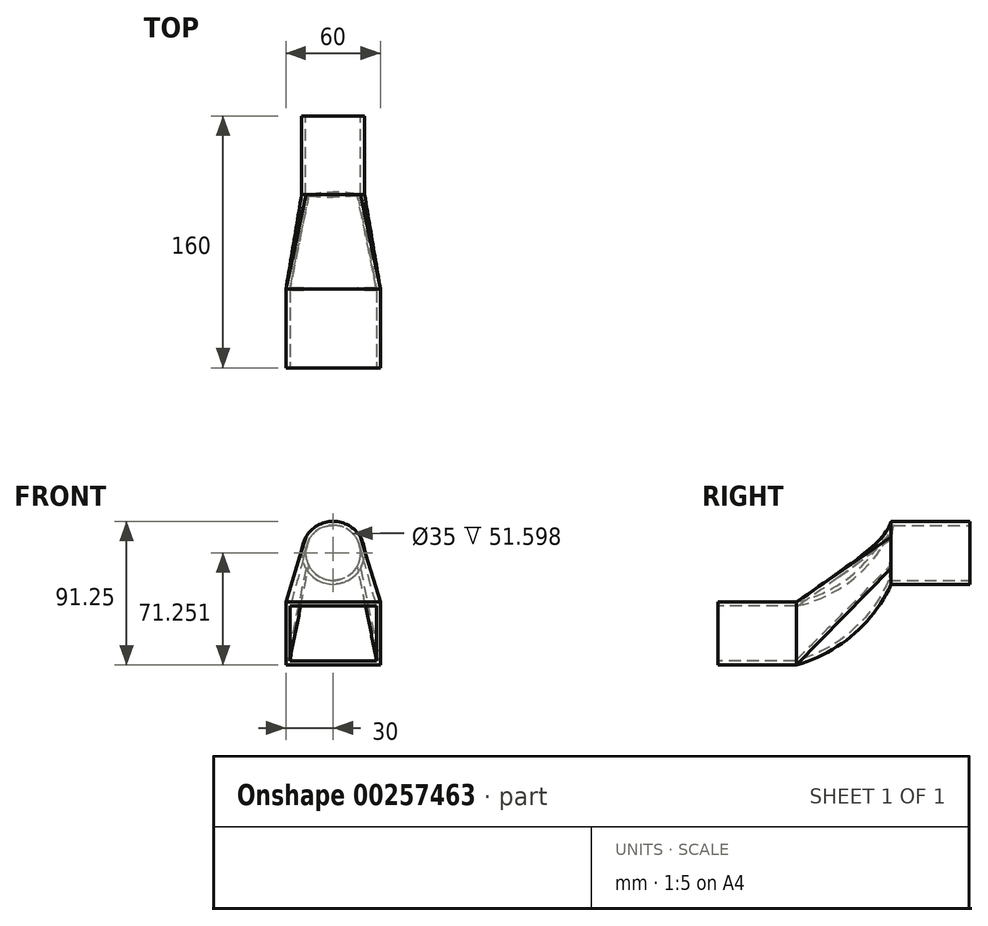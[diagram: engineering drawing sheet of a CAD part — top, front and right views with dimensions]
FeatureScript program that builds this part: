
annotation { "Feature Type Name" : "Feature", "Feature Type Description" : "" }
export const myFeature = defineFeature(function(context is Context, id is Id, definition is map)
    precondition{}
    {
        {
            var Q0;
            Q0=qCreatedBy(makeId("Front.planeOp"),FACE);
            var sketch = newSketch(context, id + "F0", { "sketchPlane" : qUnion([Q0])});
            skLineSegment(sketch, "E0.bottom", {"start": v(30, -20) * mm, "end": v(-30, -20) * mm});
            skLineSegment(sketch, "E0.top", {"start": v(30, 20) * mm, "end": v(-30, 20) * mm});
            skLineSegment(sketch, "E0.left", {"start": v(30, -20) * mm, "end": v(30, 20) * mm});
            skLineSegment(sketch, "E0.right", {"start": v(-30, -20) * mm, "end": v(-30, 20) * mm});
            skPoint(sketch, "E0.middle", {"position": v(0, 0) * mm});
            skSolve(sketch);
        }
        {
            var Q0;
            Q0=makeQuery(id+"F0.imprint","IMPRINT",FACE,{"disambiguationData":[TD([[makeQuery(id+"F0.imprint","IMPRINT",EDGE,{"derivedFrom":sQuery(id+"F0.wireOp",EDGE,"E0.bottom")}),-1.0]])]});
            extrude(context, id + "F1", {"entities" : qUnion([Q0]), "oppositeDirection" : true, "depth" : 50 * mm});
        }
        {
            var Q0;
            Q0=qCreatedBy(makeId("Front.planeOp"),FACE);
            cPlane(context, id + "F2", {"entities" : qUnion([Q0]), "cplaneType" : CPlaneType.OFFSET, "offset" : 160 * mm, "oppositeDirection" : true, "width" : 150 * mm, "height" : 150 * mm});
        }
        {
            var Q0;
            Q0=qCreatedBy(id+"F2.planeOp",FACE);
            var sketch = newSketch(context, id + "F3", { "sketchPlane" : qUnion([Q0])});
            skLineSegment(sketch, "E1.0", {"start": v(30, 20) * mm, "end": v(-30, 20) * mm, "construction": true});
            skCircle(sketch, "E2", {"center": v(0, 51.25) * mm, "radius": 20 * mm});
            skSolve(sketch);
        }
        {
            var Q0;
            Q0=makeQuery(id+"F3.imprint","IMPRINT",FACE,{"disambiguationData":[TD([[makeQuery(id+"F3.imprint","IMPRINT",EDGE,{"derivedFrom":sQuery(id+"F3.wireOp",EDGE,"E2")}),1.0]])]});
            extrude(context, id + "F4", {"entities" : qUnion([Q0]), "depth" : 50 * mm});
        }
        {
            var Q0;
            Q0=qCreatedBy(makeId("Right.planeOp"),FACE);
            var sketch = newSketch(context, id + "F5", { "sketchPlane" : qUnion([Q0])});
            skLineSegment(sketch, "E3.0.0", {"start": v(110, 31.25) * mm, "end": v(110, 71.25) * mm, "construction": true});
            skLineSegment(sketch, "E3.1.0", {"start": v(50, 20) * mm, "end": v(50, -20) * mm, "construction": true});
            skLineSegment(sketch, "E3.1.2", {"start": v(50, -20) * mm, "end": v(50, 20) * mm, "construction": true});
            skArc(sketch, "E4", {"start": v(50, 20) * mm, "mid": v(86.34, 38.2) * mm, "end": v(110, 71.25) * mm});
            skArc(sketch, "E5", {"start": v(50, -20) * mm, "mid": v(85.6, -0.93) * mm, "end": v(110, 31.25) * mm});
            skSolve(sketch);
        }
        {
            var Q1;
            Q1=makeQuery(id+"F4.opExtrude","CAP_FACE",FACE,{"disambiguationData":[OSD([sQuery(id+"F3.wireOp",EDGE,"E2")])],"isStart":false});
            var Q2;
            Q2=makeQuery(id+"F1.opExtrude","CAP_FACE",FACE,{"disambiguationData":[OSD([sQuery(id+"F0.wireOp",EDGE,"E0.bottom"),sQuery(id+"F0.wireOp",EDGE,"E0.top"),sQuery(id+"F0.wireOp",EDGE,"E0.left"),sQuery(id+"F0.wireOp",EDGE,"E0.right")])],"isStart":false});
            var Q3;
            Q3=sQuery(id+"F5.wireOp",EDGE,"E4");
            var Q4;
            Q4=sQuery(id+"F5.wireOp",EDGE,"E5");
            loft(context, id + "F6", {"operationType" : NewBodyOperationType.ADD, "addGuides" : true, "sheetProfilesArray" : [{ "sheetProfileEntities" : qUnion([Q1]) }, { "sheetProfileEntities" : qUnion([Q2]) }], "guidesArray" : [{ "guideEntities" : qUnion([Q3]), "guideDerivativeType" : LoftGuideDerivativeType.DEFAULT, "guideDerivativeMagnitude" : 1 }, { "guideEntities" : qUnion([Q4]), "guideDerivativeType" : LoftGuideDerivativeType.DEFAULT, "guideDerivativeMagnitude" : 1 }]});
        }
        {
            var Q0;
            Q0=makeQuery(id+"F4.opExtrude","CAP_FACE",FACE,{"disambiguationData":[OSD([sQuery(id+"F3.wireOp",EDGE,"E2")])],"isStart":true});
            var Q1;
            Q1=makeQuery(id+"F1.opExtrude","CAP_FACE",FACE,{"disambiguationData":[OSD([sQuery(id+"F0.wireOp",EDGE,"E0.bottom"),sQuery(id+"F0.wireOp",EDGE,"E0.top"),sQuery(id+"F0.wireOp",EDGE,"E0.left"),sQuery(id+"F0.wireOp",EDGE,"E0.right")])],"isStart":true});
            shell(context, id + "F7", {"entities" : qUnion([Q0, Q1]), "thickness" : 2.5 * mm});
        }
    });
